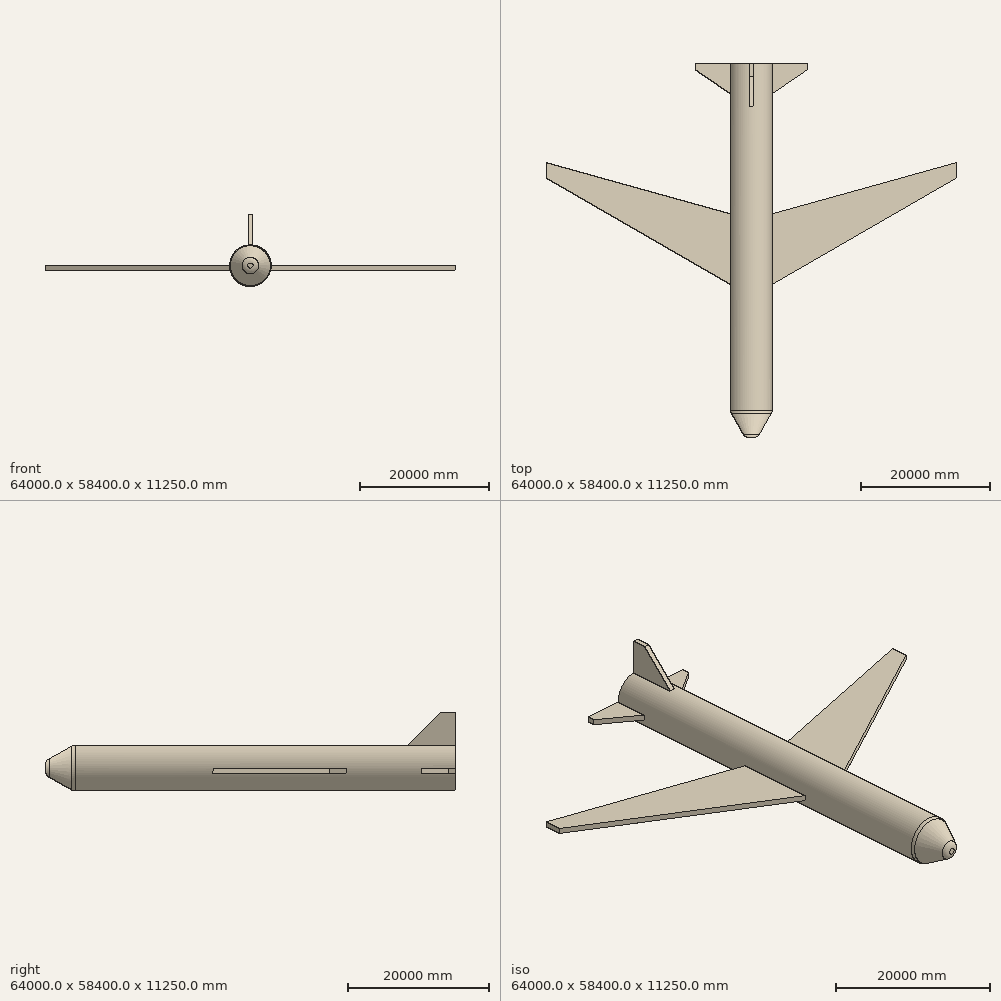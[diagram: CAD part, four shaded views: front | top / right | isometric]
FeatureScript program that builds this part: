
annotation { "Feature Type Name" : "Feature", "Feature Type Description" : "" }
export const myFeature = defineFeature(function(context is Context, id is Id, definition is map)
    precondition{}
    {
        {
            var Q0;
            Q0=qCreatedBy(makeId("Front.planeOp"),FACE);
            var sketch = newSketch(context, id + "F0", { "sketchPlane" : qUnion([Q0])});
            skCircle(sketch, "E0", {"center": v(0, 0) * mm, "radius": 3250 * mm});
            skSolve(sketch);
        }
        {
            var Q0;
            Q0=qSketchRegion(id+"F0",true);
            extrude(context, id + "F1", {"entities" : qUnion([Q0]), "oppositeDirection" : true, "depth" : 54400 * mm});
        }
        {
            var Q0;
            Q0=makeQuery(id+"F1.opExtrude","CAP_FACE",FACE,{"disambiguationData":[OSD([sQuery(id+"F0.wireOp",EDGE,"E0")])],"isStart":true});
            cPlane(context, id + "F2", {"entities" : qUnion([Q0]), "cplaneType" : CPlaneType.OFFSET, "offset" : 4000 * mm, "width" : 152.4 * mm, "height" : 152.4 * mm});
        }
        {
            var Q0;
            Q0=qCreatedBy(id+"F2.planeOp",FACE);
            var sketch = newSketch(context, id + "F3", { "sketchPlane" : qUnion([Q0])});
            skCircle(sketch, "E1", {"center": v(0, 0) * mm, "radius": 1000 * mm});
            skSolve(sketch);
        }
        {
            var Q1;
            Q1=makeQuery(id+"F1.opExtrude","CAP_FACE",FACE,{"disambiguationData":[OSD([sQuery(id+"F0.wireOp",EDGE,"E0")])],"isStart":true});
            var Q2;
            Q2=makeQuery(id+"F3.imprint","IMPRINT",FACE,{"disambiguationData":[TD([[makeQuery(id+"F3.imprint","IMPRINT",EDGE,{"derivedFrom":sQuery(id+"F3.wireOp",EDGE,"E1")}),1.0]])]});
            loft(context, id + "F4", {"operationType" : NewBodyOperationType.ADD, "sheetProfilesArray" : [{ "sheetProfileEntities" : qUnion([Q1]) }, { "sheetProfileEntities" : qUnion([Q2]) }]});
        }
        {
            var Q0;
            Q0=makeQuery(id+"F4.opLoft","MID_CAP_EDGE",EDGE,{"disambiguationData":[OSD([sQuery(id+"F0.wireOp",EDGE,"E0"),sQuery(id+"F3.wireOp",EDGE,"E1")])],"capPos":1.0});
            var Q1;
            {var subQ0=sQuery(id+"F0.wireOp",EDGE,"E0");Q1=makeQuery(id+"F4.boolean.opBoolean","MERGE",EDGE,{"derivedFrom":[makeQuery(id+"F1.opExtrude","CAP_EDGE",EDGE,{"disambiguationData":[OSD([subQ0])],"isStart":true}),makeQuery(id+"F4.opLoft","MID_CAP_EDGE",EDGE,{"disambiguationData":[OSD([subQ0])],"capPos":0.0})]});}
            fillet(context, id + "F5", {"entities" : qUnion([Q0, Q1]), "radius" : 1000 * mm, "tangentPropagation" : true, "allowEdgeOverflow" : false});
        }
        {
            var Q0;
            Q0=qCreatedBy(makeId("Right.planeOp"),FACE);
            var sketch = newSketch(context, id + "F6", { "sketchPlane" : qUnion([Q0])});
            skLineSegment(sketch, "E2", {"start": v(54400, 0) * mm, "end": v(54400, 8000) * mm});
            skLineSegment(sketch, "E3", {"start": v(54400, 8000) * mm, "end": v(52400, 8000) * mm});
            skLineSegment(sketch, "E4", {"start": v(52400, 8000) * mm, "end": v(44400, 0) * mm});
            skLineSegment(sketch, "E5", {"start": v(44400, 0) * mm, "end": v(54400, 0) * mm});
            skSolve(sketch);
        }
        {
            var Q0;
            Q0=makeQuery(id+"F6.imprint","IMPRINT",FACE,{"disambiguationData":[TD([[makeQuery(id+"F6.imprint","IMPRINT",EDGE,{"derivedFrom":sQuery(id+"F6.wireOp",EDGE,"E2")}),1.0]])]});
            extrude(context, id + "F7", {"entities" : qUnion([Q0]), "operationType" : NewBodyOperationType.ADD, "endBound" : BoundingType.SYMMETRIC, "depth" : 750 * mm});
        }
        {
            var Q0;
            Q0=qCreatedBy(makeId("Top.planeOp"),FACE);
            var sketch = newSketch(context, id + "F8", { "sketchPlane" : qUnion([Q0])});
            skLineSegment(sketch, "E6", {"start": v(0, 0) * mm, "end": v(0, 30000) * mm});
            skLineSegment(sketch, "E7", {"start": v(0, 30000) * mm, "end": v(32000, 38900.4) * mm});
            skLineSegment(sketch, "E8", {"start": v(32000, 38900.4) * mm, "end": v(32000, 36475.2) * mm});
            skLineSegment(sketch, "E9", {"start": v(32000, 36475.2) * mm, "end": v(0, 18000) * mm});
            skSolve(sketch);
        }
        {
            var Q0;
            Q0=qSketchRegion(id+"F8",true);
            extrude(context, id + "F9", {"entities" : qUnion([Q0]), "operationType" : NewBodyOperationType.ADD, "oppositeDirection" : true, "depth" : 750 * mm});
        }
        {
            var Q0;
            Q0=qCreatedBy(makeId("Top.planeOp"),FACE);
            var sketch = newSketch(context, id + "F10", { "sketchPlane" : qUnion([Q0])});
            skLineSegment(sketch, "E10", {"start": v(0, 0) * mm, "end": v(0, 54400) * mm});
            skLineSegment(sketch, "E11", {"start": v(0, 47400) * mm, "end": v(8763.2, 53400) * mm});
            skLineSegment(sketch, "E12", {"start": v(8763.2, 53400) * mm, "end": v(8763.2, 54400) * mm});
            skLineSegment(sketch, "E13", {"start": v(8763.2, 54400) * mm, "end": v(0, 54400) * mm});
            skSolve(sketch);
        }
        {
            var Q0;
            Q0 = qSketchRegion(id + "F10", true);
            extrude(context, id + "F11", {"entities" : qUnion([Q0]), "operationType" : NewBodyOperationType.ADD, "oppositeDirection" : true, "depth" : 750 * mm});
        }
        {
            var Q0;
            Q0=makeQuery(id+"F1.opExtrude","SWEPT_BODY",BODY,{"disambiguationData":[OSD([sQuery(id+"F0.wireOp",EDGE,"E0")])]});
            var Q1;
            Q1=qCreatedBy(makeId("Right.planeOp"),FACE);
            mirror(context, id + "F12", {"operationType" : NewBodyOperationType.ADD, "entities" : qUnion([Q0]), "mirrorPlane" : qUnion([Q1])});
        }
    });
